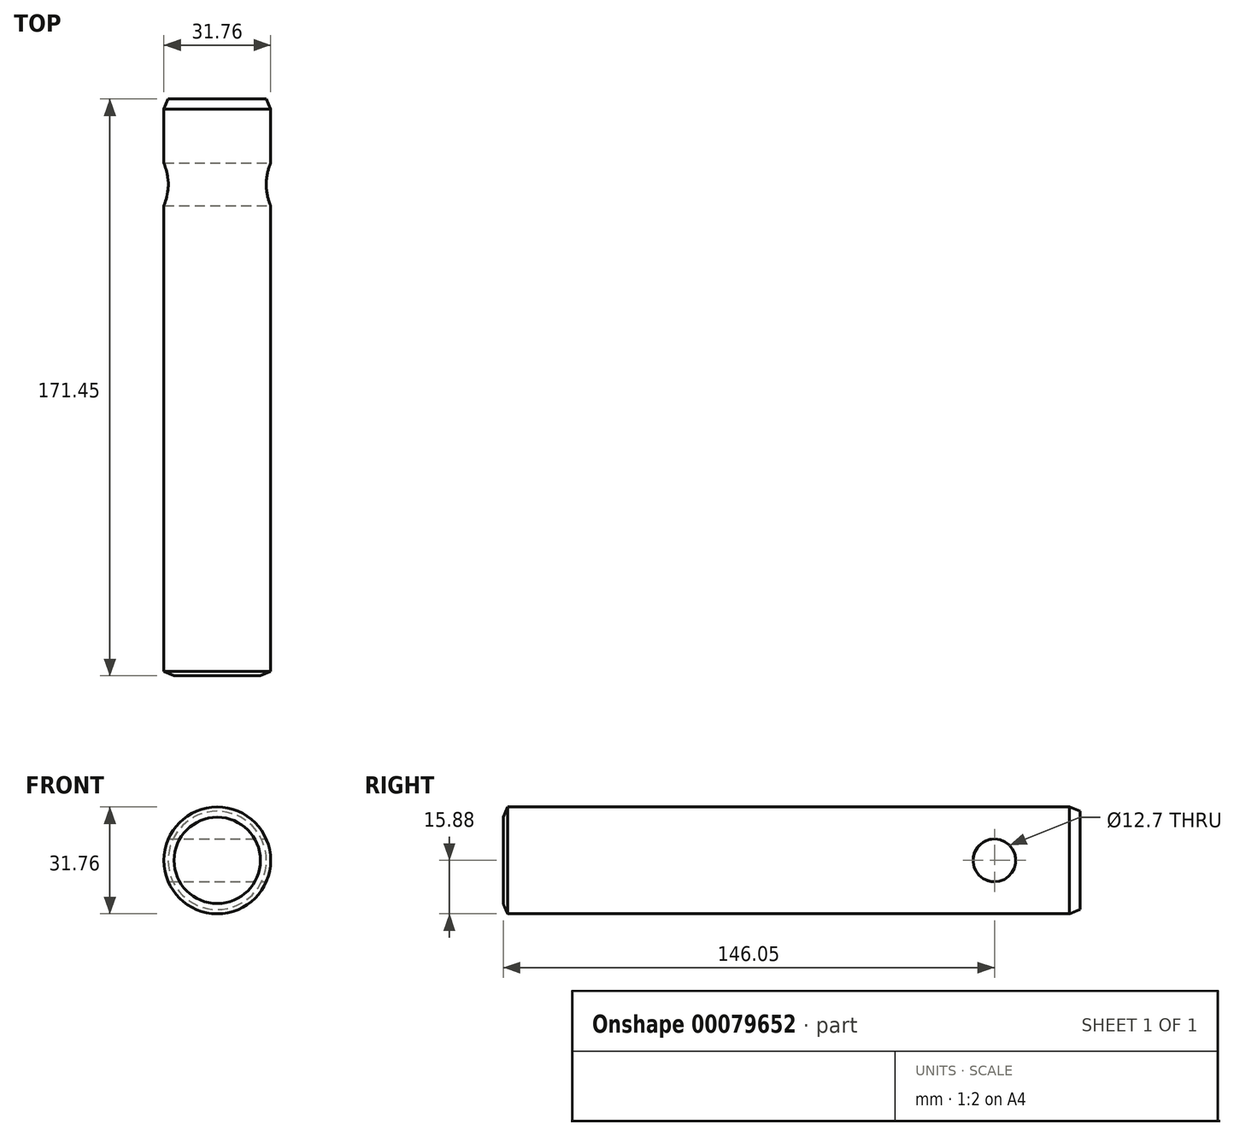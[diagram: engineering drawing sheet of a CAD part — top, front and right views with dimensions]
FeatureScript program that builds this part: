
annotation { "Feature Type Name" : "Feature", "Feature Type Description" : "" }
export const myFeature = defineFeature(function(context is Context, id is Id, definition is map)
    precondition{}
    {
        {
            var Q0;
            Q0=qCreatedBy(makeId("Front.planeOp"),FACE);
            var sketch = newSketch(context, id + "F0", { "sketchPlane" : qUnion([Q0])});
            skCircle(sketch, "E0", {"center": v(0, 0) * mm, "radius": 15.88 * mm});
            skSolve(sketch);
        }
        {
            var Q0;
            Q0=makeQuery(id+"F0.imprint","IMPRINT",FACE,{"disambiguationData":[TD([[makeQuery(id+"F0.imprint","IMPRINT",EDGE,{"derivedFrom":sQuery(id+"F0.wireOp",EDGE,"E0")}),1.0]])]});
            extrude(context, id + "F1", {"entities" : qUnion([Q0]), "depth" : 171.45 * mm});
        }
        {
            var Q0;
            Q0=qCreatedBy(makeId("Right.planeOp"),FACE);
            var sketch = newSketch(context, id + "F2", { "sketchPlane" : qUnion([Q0])});
            skCircle(sketch, "E1", {"center": v(-25.4, 0) * mm, "radius": 6.35 * mm});
            skSolve(sketch);
        }
        {
            var Q0;
            Q0 = qSketchRegion(id + "F2", true);
            extrude(context, id + "F3", {"entities" : qUnion([Q0]), "operationType" : NewBodyOperationType.REMOVE, "oppositeDirection" : true, "depth" : 25.4 * mm});
        }
        {
            var Q0;
            Q0=makeQuery(id+"F3.boolean.opBoolean","COPY",FACE,{"derivedFrom":makeQuery(id+"F3.opExtrude","CAP_FACE",FACE,{"disambiguationData":[OSD([sQuery(id+"F2.wireOp",EDGE,"E1")])],"isStart":true})});
            extrude(context, id + "F4", {"entities" : qUnion([Q0]), "operationType" : NewBodyOperationType.REMOVE, "oppositeDirection" : true, "depth" : 25.4 * mm});
        }
        {
            var Q0;
            Q0=makeQuery(id+"F1.opExtrude","CAP_EDGE",EDGE,{"disambiguationData":[OSD([sQuery(id+"F0.wireOp",EDGE,"E0")])],"isStart":false});
            chamfer(context, id + "F5", {"entities" : qUnion([Q0]), "chamferType" : ChamferType.TWO_OFFSETS, "width1" : 1.27 * mm, "oppositeDirection" : false, "width2" : 3.05 * mm, "tangentPropagation" : true});
        }
        {
            var Q0;
            Q0=makeQuery(id+"F1.opExtrude","CAP_EDGE",EDGE,{"disambiguationData":[OSD([sQuery(id+"F0.wireOp",EDGE,"E0")])],"isStart":true});
            chamfer(context, id + "F6", {"entities" : qUnion([Q0]), "chamferType" : ChamferType.TWO_OFFSETS, "width1" : 1.27 * mm, "oppositeDirection" : true, "width2" : 3.05 * mm, "tangentPropagation" : true});
        }
    });
